# Revit family: P4D22
name_source: partatom
category: Lighting Fixtures
revit_build: Autodesk Revit Architecture 2012 (Build: 20110309_2315(x64)
units: mm (PartAtom-declared; Revit-internal decimal feet)

## types (7) — shared parameters
Airtight = Black
Apparent Load = 0 VA
Color Filter = 16777215
Default Elevation = 48"
Description = High Efficiency Static Parabolic
Dimming Lamp Color Temperature Shift = <None>
Emit from Line Length = 24"
Finish = Steel
Glass = Glass
Lamp = Two or Four
Manufacturer = Columbia Lighting
Manufacturer Fax = (864)-678-1065
Model = P4D22_2
Product Page URL = http://www.columbialighting.com
Product Specification Sheet = http://www.columbialighting.com
Tilt Angle = 90.00°
URL = http://www.columbialighting.com
Wattage Comments = 25-54 W

## per-type parameters (varying)
| type | Photometric Web File |
| P4D22-232U6G-MA33 | 12476 |
| P4D22-240TT-MA33 | 12469 |
| P4D22-317G-MA33-S | 13230 |
| P4D22-331U1-MA33 | 12463 |
| P4D22-340TT-MA33 | 12474 |
| P4D22-417G-MA44 | 13172 |
| type_6 |  |

## geometry (parser evidence)
native form markers: Blend x2, Sweep x1
no freeform markers — native parametric forms only
